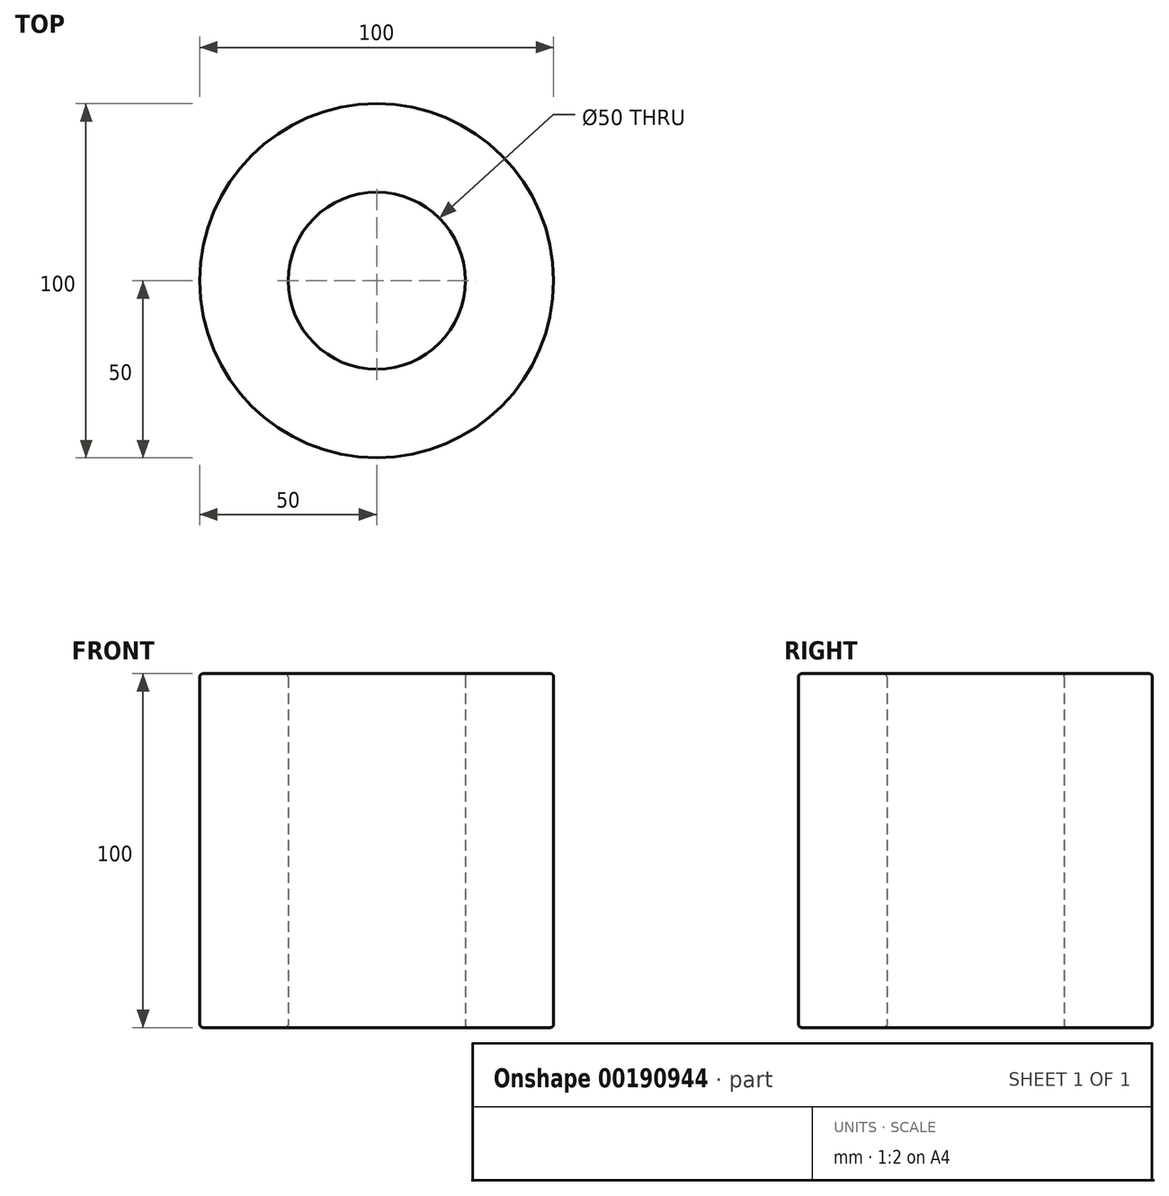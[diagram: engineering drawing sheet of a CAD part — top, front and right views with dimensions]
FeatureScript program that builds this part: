
annotation { "Feature Type Name" : "Feature", "Feature Type Description" : "" }
export const myFeature = defineFeature(function(context is Context, id is Id, definition is map)
    precondition{}
    {
        {
            var Q0;
            Q0=qCreatedBy(makeId("Top.planeOp"),FACE);
            var sketch = newSketch(context, id + "F0", { "sketchPlane" : qUnion([Q0])});
            skCircle(sketch, "E0", {"center": v(0, 0) * mm, "radius": 50 * mm});
            skSolve(sketch);
        }
        {
            var Q0;
            Q0 = qSketchRegion(id + "F0", true);
            extrude(context, id + "F1", {"entities" : qUnion([Q0]), "depth" : 100 * mm});
        }
        {
            var Q0;
            Q0=makeQuery(id+"F1.opExtrude","CAP_FACE",FACE,{"disambiguationData":[OSD([sQuery(id+"F0.wireOp",EDGE,"E0")])],"isStart":false});
            var Q1;
            Q1=makeQuery(id+"F1.opExtrude","CAP_FACE",FACE,{"disambiguationData":[OSD([sQuery(id+"F0.wireOp",EDGE,"E0")])],"isStart":true});
            shell(context, id + "F2", {"entities" : qUnion([Q0, Q1]), "thickness" : 25 * mm});
        }
        {
            var Q0;
            Q0=makeQuery(id+"F1.opExtrude","CAP_FACE",FACE,{"disambiguationData":[OSD([sQuery(id+"F0.wireOp",EDGE,"E0")])],"isStart":false});
            var Q1;
            Q1=makeQuery(id+"F1.opExtrude","CAP_FACE",FACE,{"disambiguationData":[OSD([sQuery(id+"F0.wireOp",EDGE,"E0")])],"isStart":true});
            fillet(context, id + "F3", {"entities" : qUnion([Q0, Q1]), "radius" : 1 * mm, "tangentPropagation" : true, "allowEdgeOverflow" : false});
        }
    });
